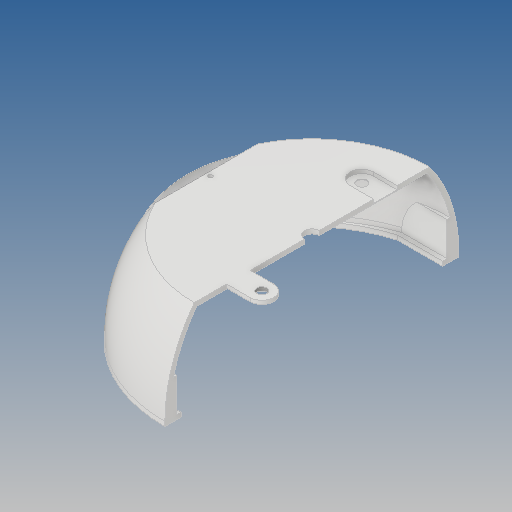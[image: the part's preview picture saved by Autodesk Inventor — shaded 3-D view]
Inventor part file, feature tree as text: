
AUTODESK INVENTOR PART (.ipt)
format: ipt  version: 2020 (Build 240168000, 168)  size: 686,592 bytes
history: native  units: mm
features: sketch x35, extrude x31, other x10, projected_geometry x6, hole x4, reference x2, revolve x1, loft x1, shell x1, mirror x1, fillet x1
ambient origin geometry x8: Origin, YZ Plane, XZ Plane, XY Plane, X Axis, Y Axis, Z Axis, Center Point
bodies: Body1 (feature_tree)
feature tree (93):
  revolve  "Вращение3"
  extrude  "Выдавливание106"  Depth=170.0mm
  extrude  "Выдавливание107"  Depth=100.0mm
  hole  "Отверстие2"  [1 undecoded]
  extrude  "Выдавливание108"  Depth=4.0mm
  hole  "Отверстие3"  [1 undecoded]
  hole  "Отверстие4"  [1 undecoded]
  hole  "Отверстие5"  [1 undecoded]
  extrude  "Выдавливание109"  TaperAngle=0.0deg  [1 undecoded]
  sketch  "Эскиз132"
  extrude  "Выдавливание110"  Depth=130.0mm TaperAngle=0.0deg
  extrude  "Выдавливание111"  Depth=5.0mm
  extrude  "Выдавливание113"  Depth=2.0mm
  extrude  "Выдавливание114"  Depth=2.0mm
  other  "РабПлоскость27"
  extrude  "Выдавливание115"  Depth=2.0mm
  extrude  "Выдавливание116"  Depth=20.0mm
  extrude  "Выдавливание117"  Depth=10.0mm TaperAngle=0.0deg
  sketch  "Эскиз4"
  other  "РабПлоскость1"
  sketch  "Эскиз5"
  loft  "Лофт1"
  extrude  "Выдавливание2"  Depth=143.802871mm
  shell  "Оболочка1"  Thickness=0.0mm
  sketch  "Эскиз21"
  extrude  "Выдавливание15"  Depth=1.0mm TaperAngle=0.0deg
  extrude  "Выдавливание16"  Depth=5.0mm
  other  "РабПлоскость7"
  sketch  "Эскиз23"
  extrude  "Выдавливание17"  Depth=5.0mm
  extrude  "Выдавливание18"  Depth=2.0mm
  sketch  "Эскиз24"
  extrude  "Выдавливание19"  Depth=2.0mm
  extrude  "Выдавливание20"  Depth=5.0mm
  extrude  "Выдавливание21"  Depth=1.0mm TaperAngle=0.0deg
  mirror  "Зеркальное отражение2"
  other  "РабПлоскость12"
  sketch  "Эскиз42"
  extrude  "Выдавливание57"  Depth=3.0mm
  sketch  "Эскиз84"
  extrude  "Выдавливание75"  Depth=2.0mm
  extrude  "Выдавливание76"  Depth=6.0mm
  extrude  "Выдавливание77"  Depth=1.0mm TaperAngle=0.0deg
  extrude  "Выдавливание95"  Depth=2.0mm
  extrude  "Выдавливание96"  Depth=2.0mm
  extrude  "Выдавливание97"  Depth=2.0mm
  fillet  "Сопряжение3"  Radius=5.0mm
  extrude  "Выдавливание98"  Depth=1.0mm TaperAngle=0.0deg
  extrude  "Выдавливание101"  Depth=4.0mm
  other  "РабПлоскость25"
  extrude  "Выдавливание102"  Depth=2.0mm
  other  "РабПлоскость26"
  extrude  "Выдавливание103"  Depth=2.0mm
  extrude  "Выдавливание104"  Depth=2.0mm
  sketch  "Эскиз6"
  projected_geometry  "Спроецированная петля1"
  sketch  "Эскиз22"
  sketch  "Эскиз25"
  sketch  "Эскиз61"
  sketch  "Эскиз87"
  sketch  "Эскиз109"
  sketch  "Эскиз110"
  projected_geometry  "Спроецированная петля42"
  sketch  "Эскиз111"
  projected_geometry  "Спроецированная петля43"
  sketch  "Эскиз114"
  sketch  "Эскиз117"
  sketch  "Эскиз118"
  reference  "Ссылка1"
  reference  "Ссылка2"
  sketch  "Эскиз119"
  sketch  "Эскиз120"
  sketch  "Эскиз121"
  other  "Твердое тело3"
  sketch  "Эскиз124"
  sketch  "Эскиз125"
  sketch  "Эскиз126"
  sketch  "Эскиз127"
  sketch  "Эскиз128"
  sketch  "Эскиз129"
  sketch  "Эскиз130"
  sketch  "Эскиз131"
  projected_geometry  "Спроецированная петля45"
  projected_geometry  "Спроецированная петля46"
  sketch  "Эскиз133"
  sketch  "Эскиз134"
  sketch  "Эскиз135"
  sketch  "Эскиз136"
  projected_geometry  "Спроецированная петля47"
  sketch  "Эскиз137"
  other  "<userpath>\Desktop\САПР\Работы\ПД\робот\робот - сборка фулл.iam"
  other  "робот - сборка фулл.iam"
  other  "крепление-стенки:1"
note: 5 required parameter values undecoded (feature->parameter linkage not recoverable at this tier; creation-order binding heuristic only, values carry confidence <= 0.55)
